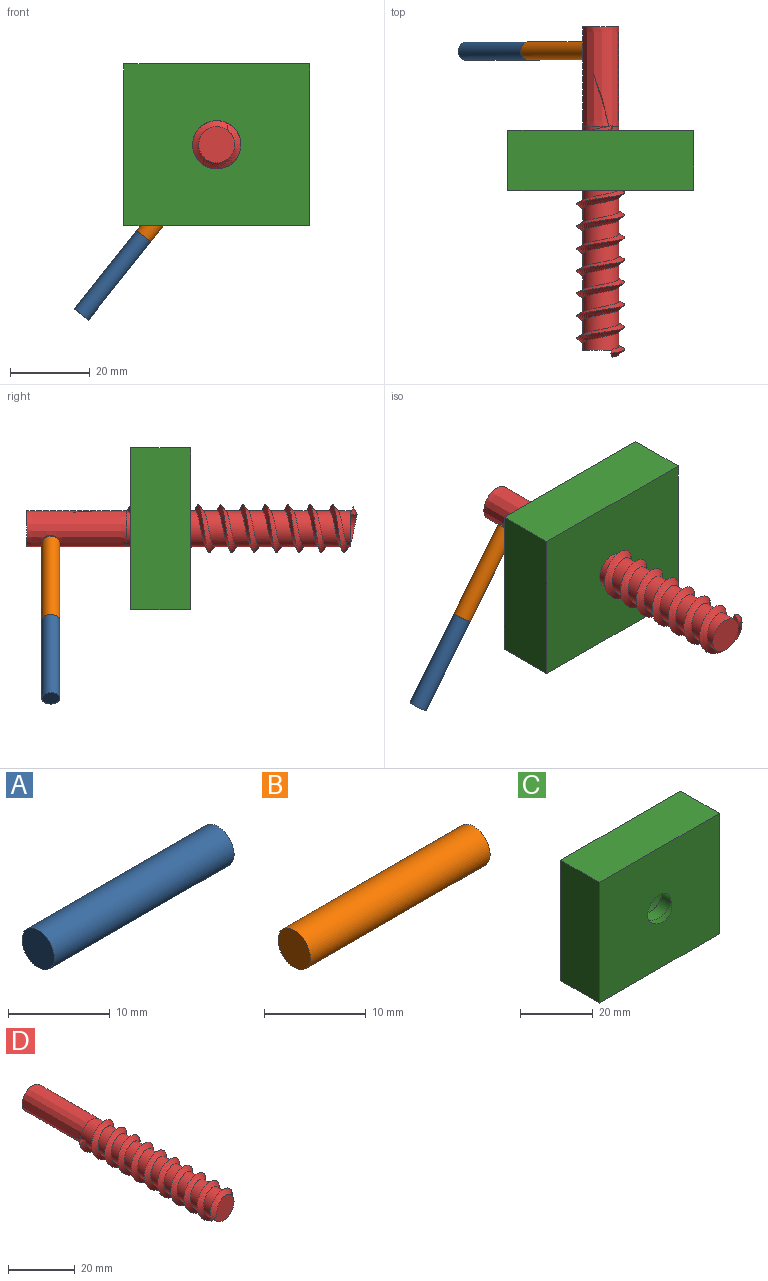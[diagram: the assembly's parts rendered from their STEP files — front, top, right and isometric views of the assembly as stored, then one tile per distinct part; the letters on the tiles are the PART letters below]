
ASSEMBLY  parts=4 mates=3
PART A: 3 faces, bbox 25x4.5x4.5 mm
  f0: cylinder r=2.26mm len=25mm, axis (-1,0,0), area 354.5mm2, adj f1,f2
  f1: plane 4.51x4.51mm, normal (1,0,0), area 16mm2, adj f0
  f2: plane 4.51x4.51mm, normal (-1,0,0), area 16mm2, adj f0
PART B: 3 faces, bbox 25x4.5x4.5 mm
  f0: cylinder r=2.26mm len=25mm, axis (-1,0,0), area 354.5mm2, adj f1,f2
  f1: plane 4.51x4.51mm, normal (1,0,0), area 16mm2, adj f0
  f2: plane 4.51x4.51mm, normal (-1,0,0), area 16mm2, adj f0
PART C: 9 faces, bbox 46.9x19.2x40.9 mm
  f0: plane 46.43x15mm, normal (0,0,1), area 696.5mm2, adj f2,f3,f4,f8
  f1: plane 46.43x15mm, normal (0,0,-1), area 696.5mm2, adj f2,f3,f4,f8
  f2: plane 46.83x40.82mm, normal (0,-1,0), area 1804.7mm2, adj f0,f1,f3,f4,f5,f6,f7
  f3: plane 40.42x15mm, normal (1,0,0), area 606.3mm2, adj f0,f1,f2,f8
  f4: plane 40.42x15mm, normal (-1,0,0), area 606.3mm2, adj f0,f1,f2,f8
  f5: bspline ~18.73x13.48mm, area 152.8mm2, adj f2,f6,f7,f8
  f6: cylinder r=4.51mm len=15mm, axis (0,1,0), area 273mm2, adj f2,f5,f7,f8
  f7: bspline ~17.8x13.48mm, area 173.6mm2, adj f2,f5,f6,f8
  f8: plane 46.86x40.85mm, normal (0,1,0), area 1804.7mm2, adj f0,f1,f3,f4,f5,f6,f7
PART D: 11 faces, bbox 13.5x82.8x13.6 mm
  f0: extruded ~25x9.02mm, area 698.8mm2, adj f1,f5,f6,f8,f9
  f1: cylinder r=4.51mm len=56mm, axis (0,1,0), area 1090.8mm2, adj f0,f2,f4,f5,f6,f7
  f2: plane 9.04x9.04mm, normal (0,-1,0), area 63.9mm2, adj f1,f3
  f3: cylinder r=4.5mm len=6.19mm, axis (0,1,0), area 7.6mm2, adj f2,f4,f7
  f4: plane 2.01x1.5mm, normal (0.74,0,-0.67), area 2mm2, adj f1,f3,f6,f7
  f5: plane 2.01x1.5mm, normal (-0.74,0,0.67), area 2mm2, adj f0,f1,f6,f7
  f6: bspline ~57x13.48mm, area 567.7mm2, adj f0,f1,f4,f5,f7
  f7: bspline ~57x12.04mm, area 646.7mm2, adj f1,f3,f4,f5,f6
  f8: plane 9.1x9.1mm, normal (0,1,0), area 64mm2, adj f0
  f9: cylinder r=2.26mm len=4.51mm, axis (-1,0,0), area 55.4mm2, adj f0,f10
  f10: plane 4.51x4.51mm, normal (1,0,0), area 16mm2, adj f9
PLACE A rot(axis=(-0.46,-0.86,-0.22),58.5deg) t=(-56.56,-6.66,-56.29)mm
PLACE B rot(axis=(0,-1,0),51.4deg) t=(-18.25,-9,-22.89)mm
PLACE C at identity fixed
PLACE D rot(axis=(0,1,0),128.6deg) t=(0,-9,0)mm
MATE slider D.f9 <-> B.f0  axis (0.62,0,0.78) through (-1.42,9.94,-1.78)mm
MATE cylindrical D.f1 <-> C.f6  axis (0,-1,0) through (0,-65,0)mm
MATE revolute A.f0 <-> B.f0  axis (0.62,0,0.78) through (-18.25,9.94,-22.89)mm
